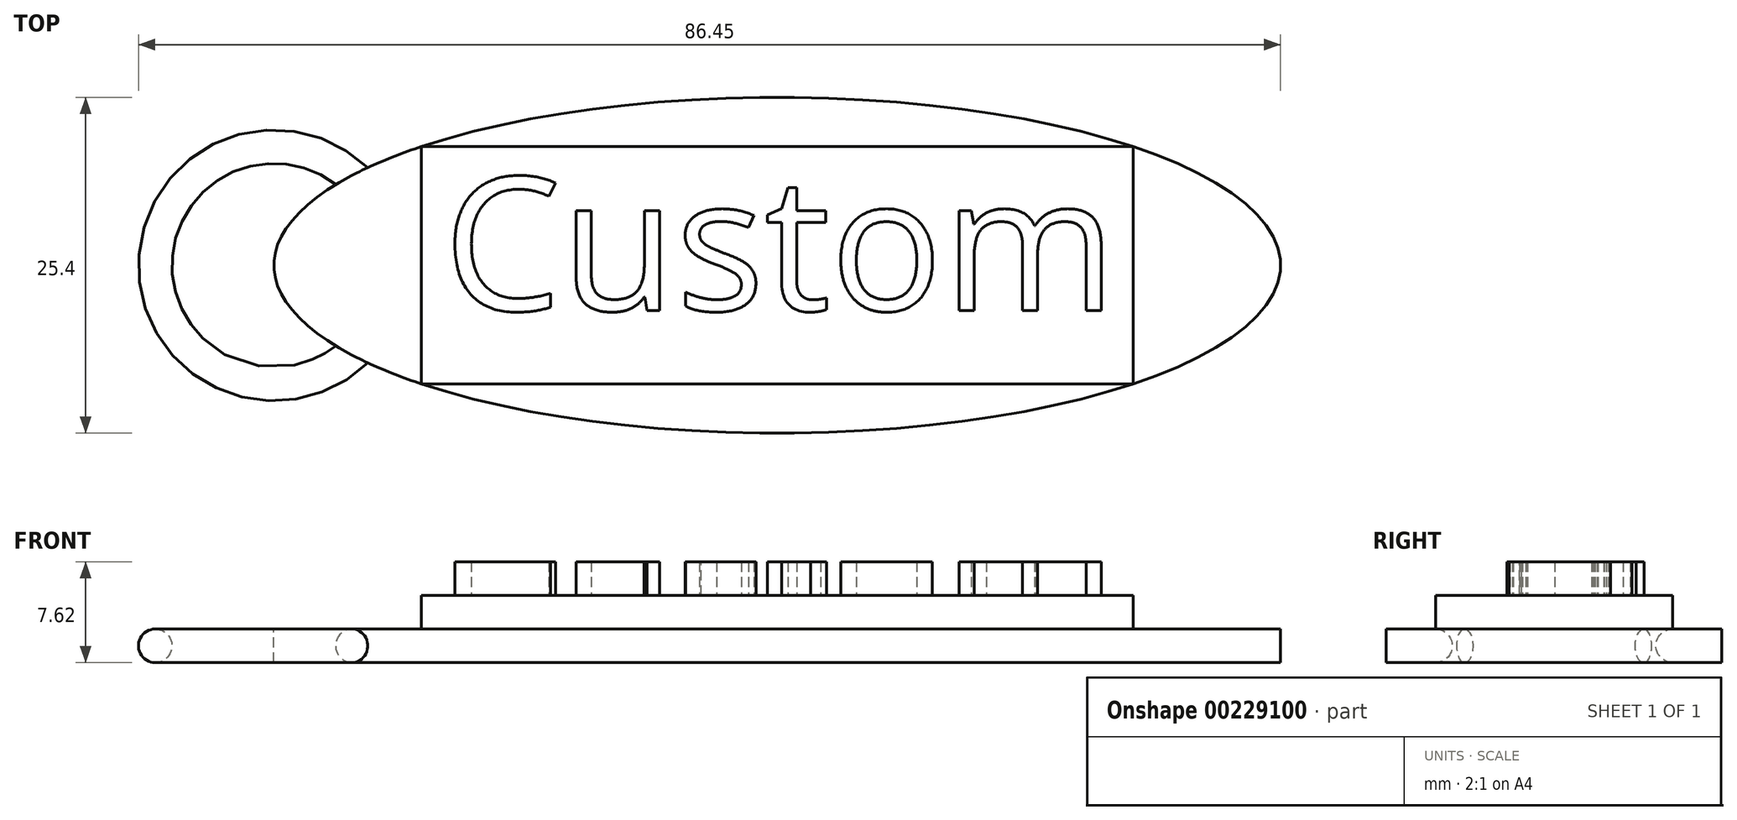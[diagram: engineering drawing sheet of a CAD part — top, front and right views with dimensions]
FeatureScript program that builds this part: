
annotation { "Feature Type Name" : "Feature", "Feature Type Description" : "" }
export const myFeature = defineFeature(function(context is Context, id is Id, definition is map)
    precondition{}
    {
        {
            var Q0;
            Q0=qCreatedBy(makeId("Top.planeOp"),FACE);
            var sketch = newSketch(context, id + "F0", { "sketchPlane" : qUnion([Q0])});
            skLineSegment(sketch, "E0", {"start": v(0, 0) * mm, "end": v(0, 12.7) * mm, "construction": true});
            skLineSegment(sketch, "E1", {"start": v(0, 0) * mm, "end": v(0, -12.7) * mm, "construction": true});
            skLineSegment(sketch, "E2", {"start": v(0, 0) * mm, "end": v(38.1, 0) * mm, "construction": true});
            skLineSegment(sketch, "E3", {"start": v(0, 0) * mm, "end": v(-38.1, 0) * mm, "construction": true});
            skEllipse(sketch, "E4", {"center": v(0, 0) * mm, "majorRadius": 38.1 * mm, "minorRadius": 12.7 * mm, "majorAxis": v(1, 0)});
            skPoint(sketch, "E5", {"position": v(-38.1, 0) * mm});
            skSolve(sketch);
        }
        {
            var Q0;
            Q0=makeQuery(id+"F0.imprint","IMPRINT",FACE,{"disambiguationData":[TD([[makeQuery(id+"F0.imprint","IMPRINT",EDGE,{"derivedFrom":sQuery(id+"F0.wireOp",EDGE,"E4")}),1.0]])]});
            extrude(context, id + "F1", {"entities" : qUnion([Q0]), "depth" : 2.54 * mm});
        }
        {
            var Q0;
            Q0=makeQuery(id+"F1.opExtrude","CAP_FACE",FACE,{"disambiguationData":[OSD([sQuery(id+"F0.wireOp",EDGE,"E4")])],"isStart":false});
            var sketch = newSketch(context, id + "F2", { "sketchPlane" : qUnion([Q0])});
            skLineSegment(sketch, "E6", {"start": v(0, 0) * mm, "end": v(-38.1, 0) * mm, "construction": true});
            skLineSegment(sketch, "E7", {"start": v(-38.1, 0) * mm, "end": v(38.1, 0) * mm, "construction": true});
            skLineSegment(sketch, "E8", {"start": v(0, 0) * mm, "end": v(0, 12.7) * mm, "construction": true});
            skLineSegment(sketch, "E9", {"start": v(0, 12.7) * mm, "end": v(0, -12.7) * mm, "construction": true});
            skLineSegment(sketch, "E10", {"start": v(-38.1, 0) * mm, "end": v(0, 12.7) * mm, "construction": true});
            skLineSegment(sketch, "E11", {"start": v(0, 12.7) * mm, "end": v(38.1, 0) * mm, "construction": true});
            skLineSegment(sketch, "E12", {"start": v(38.1, 0) * mm, "end": v(0, -12.7) * mm, "construction": true});
            skLineSegment(sketch, "E13", {"start": v(0, -12.7) * mm, "end": v(-38.1, 0) * mm, "construction": true});
            skLineSegment(sketch, "E14", {"start": v(0, 0) * mm, "end": v(26.94, -8.98) * mm, "construction": true});
            skLineSegment(sketch, "E15", {"start": v(26.94, -8.98) * mm, "end": v(26.94, 8.98) * mm});
            skLineSegment(sketch, "E16", {"start": v(26.94, 8.98) * mm, "end": v(-26.94, 8.98) * mm});
            skLineSegment(sketch, "E17", {"start": v(-26.94, 8.98) * mm, "end": v(-26.94, -8.98) * mm});
            skLineSegment(sketch, "E18", {"start": v(-26.94, -8.98) * mm, "end": v(26.94, -8.98) * mm});
            skSolve(sketch);
        }
        {
            var Q0;
            Q0=makeQuery(id+"F2.imprint","IMPRINT",FACE,{"disambiguationData":[TD([[makeQuery(id+"F2.imprint","IMPRINT",EDGE,{"derivedFrom":sQuery(id+"F2.wireOp",EDGE,"E15")}),1.0]])]});
            extrude(context, id + "F3", {"entities" : qUnion([Q0]), "operationType" : NewBodyOperationType.ADD, "depth" : 2.54 * mm});
        }
        {
            var Q0;
            Q0=makeQuery(id+"F3.opExtrude","CAP_FACE",FACE,{"disambiguationData":[OSD([sQuery(id+"F2.wireOp",EDGE,"E15"),sQuery(id+"F2.wireOp",EDGE,"E16"),sQuery(id+"F2.wireOp",EDGE,"E17"),sQuery(id+"F2.wireOp",EDGE,"E18")])],"isStart":false});
            var sketch = newSketch(context, id + "F4", { "sketchPlane" : qUnion([Q0])});
            skLineSegment(sketch, "E19", {"start": v(-26.94, 8.98) * mm, "end": v(26.94, -8.98) * mm, "construction": true});
            skLineSegment(sketch, "E20", {"start": v(-26.94, -8.98) * mm, "end": v(26.94, 8.98) * mm, "construction": true});
            skLineSegment(sketch, "E21", {"start": v(-26.94, 0) * mm, "end": v(26.94, 0) * mm, "construction": true});
            skLineSegment(sketch, "E22", {"start": v(0, 8.98) * mm, "end": v(0, -8.98) * mm, "construction": true});
            skLineSegment(sketch, "E23", {"start": v(0, 8.98) * mm, "end": v(-26.94, 0) * mm, "construction": true});
            skLineSegment(sketch, "E24", {"start": v(0, 8.98) * mm, "end": v(26.94, 0) * mm, "construction": true});
            skLineSegment(sketch, "E25", {"start": v(26.94, 0) * mm, "end": v(0, -8.98) * mm, "construction": true});
            skLineSegment(sketch, "E26", {"start": v(0, -8.98) * mm, "end": v(-26.94, 0) * mm, "construction": true});
            skLineSegment(sketch, "E27", {"start": v(-13.47, -4.5) * mm, "end": v(-13.47, -8.98) * mm, "construction": true});
            skLineSegment(sketch, "E28", {"start": v(-13.47, -8.98) * mm, "end": v(-13.47, 8.98) * mm, "construction": true});
            skLineSegment(sketch, "E29", {"start": v(13.47, -4.5) * mm, "end": v(13.47, -8.98) * mm, "construction": true});
            skLineSegment(sketch, "E30", {"start": v(13.47, -8.98) * mm, "end": v(13.47, 8.98) * mm, "construction": true});
            skLineSegment(sketch, "E31", {"start": v(13.47, 8.98) * mm, "end": v(26.94, 0) * mm, "construction": true});
            skLineSegment(sketch, "E32", {"start": v(13.47, 0) * mm, "end": v(26.94, 8.98) * mm, "construction": true});
            skLineSegment(sketch, "E33", {"start": v(26.94, 0) * mm, "end": v(13.47, -8.98) * mm, "construction": true});
            skLineSegment(sketch, "E34", {"start": v(13.47, 0) * mm, "end": v(26.94, -8.98) * mm, "construction": true});
            skLineSegment(sketch, "E35", {"start": v(-26.94, 8.98) * mm, "end": v(-13.47, 0) * mm, "construction": true});
            skLineSegment(sketch, "E36", {"start": v(-13.47, 8.98) * mm, "end": v(-26.94, 0) * mm, "construction": true});
            skLineSegment(sketch, "E37", {"start": v(-13.47, 8.98) * mm, "end": v(0, 0) * mm, "construction": true});
            skLineSegment(sketch, "E38", {"start": v(0, 8.98) * mm, "end": v(-13.47, 0) * mm, "construction": true});
            skLineSegment(sketch, "E39", {"start": v(-26.94, -8.98) * mm, "end": v(-13.47, 0) * mm, "construction": true});
            skLineSegment(sketch, "E40", {"start": v(-26.94, 0) * mm, "end": v(-13.47, -8.98) * mm, "construction": true});
            skLineSegment(sketch, "E41", {"start": v(-13.47, -8.98) * mm, "end": v(0, 0) * mm, "construction": true});
            skLineSegment(sketch, "E42", {"start": v(-13.47, 0) * mm, "end": v(0, -8.98) * mm, "construction": true});
            skLineSegment(sketch, "E43", {"start": v(0, -8.98) * mm, "end": v(13.47, 0) * mm, "construction": true});
            skLineSegment(sketch, "E44", {"start": v(0, 0) * mm, "end": v(13.47, -8.98) * mm, "construction": true});
            skLineSegment(sketch, "E45", {"start": v(0, 8.98) * mm, "end": v(13.47, 0) * mm, "construction": true});
            skLineSegment(sketch, "E46", {"start": v(13.47, 8.98) * mm, "end": v(0, 0) * mm, "construction": true});
            skLineSegment(sketch, "E47", {"start": v(-20.2, 4.5) * mm, "end": v(-20.2, 8.98) * mm, "construction": true});
            skLineSegment(sketch, "E48", {"start": v(-20.2, 8.98) * mm, "end": v(-20.2, -8.98) * mm, "construction": true});
            skLineSegment(sketch, "E49", {"start": v(-6.74, 4.5) * mm, "end": v(-6.74, 8.98) * mm, "construction": true});
            skLineSegment(sketch, "E50", {"start": v(-6.74, 8.98) * mm, "end": v(-6.74, -8.98) * mm, "construction": true});
            skLineSegment(sketch, "E51", {"start": v(6.74, -4.5) * mm, "end": v(6.74, 8.98) * mm, "construction": true});
            skLineSegment(sketch, "E52", {"start": v(6.74, 8.98) * mm, "end": v(6.74, -8.98) * mm, "construction": true});
            skLineSegment(sketch, "E53", {"start": v(20.2, -4.5) * mm, "end": v(20.2, -8.98) * mm, "construction": true});
            skLineSegment(sketch, "E54", {"start": v(20.2, -8.98) * mm, "end": v(20.2, 8.98) * mm, "construction": true});
            skLineSegment(sketch, "E55", {"start": v(20.2, 0) * mm, "end": v(26.94, 8.98) * mm, "construction": true});
            skLineSegment(sketch, "E56", {"start": v(13.47, 0) * mm, "end": v(20.2, 8.98) * mm, "construction": true});
            skLineSegment(sketch, "E57", {"start": v(20.2, 8.98) * mm, "end": v(26.94, 0) * mm, "construction": true});
            skLineSegment(sketch, "E58", {"start": v(20.2, 0) * mm, "end": v(26.94, -8.98) * mm, "construction": true});
            skLineSegment(sketch, "E59", {"start": v(26.94, 0) * mm, "end": v(20.2, -8.98) * mm, "construction": true});
            skLineSegment(sketch, "E60", {"start": v(-26.94, 0) * mm, "end": v(-20.2, -8.98) * mm, "construction": true});
            skLineSegment(sketch, "E61", {"start": v(-26.94, -8.98) * mm, "end": v(-20.2, 0) * mm, "construction": true});
            skLineSegment(sketch, "E62", {"start": v(-26.94, 8.98) * mm, "end": v(-20.2, 0) * mm, "construction": true});
            skLineSegment(sketch, "E63", {"start": v(-20.2, 8.98) * mm, "end": v(-26.94, 0) * mm, "construction": true});
            skLineSegment(sketch, "E64", {"start": v(-20.2, 4.5) * mm, "end": v(-26.94, 4.5) * mm, "construction": true});
            skLineSegment(sketch, "E65", {"start": v(-23.57, 4.5) * mm, "end": v(-23.57, 8.98) * mm, "construction": true});
            skLineSegment(sketch, "E66", {"start": v(-23.57, 8.98) * mm, "end": v(-23.57, -8.98) * mm, "construction": true});
            skLineSegment(sketch, "E67", {"start": v(-23.57, -4.5) * mm, "end": v(-26.94, -4.5) * mm, "construction": true});
            skLineSegment(sketch, "E68", {"start": v(-26.94, -4.5) * mm, "end": v(-20.2, -4.5) * mm, "construction": true});
            skLineSegment(sketch, "E69", {"start": v(23.57, 4.5) * mm, "end": v(26.94, 4.5) * mm, "construction": true});
            skLineSegment(sketch, "E70", {"start": v(26.94, 4.5) * mm, "end": v(20.2, 4.5) * mm, "construction": true});
            skLineSegment(sketch, "E71", {"start": v(23.57, 4.5) * mm, "end": v(23.57, 8.98) * mm, "construction": true});
            skLineSegment(sketch, "E72", {"start": v(23.57, 8.98) * mm, "end": v(23.57, -8.98) * mm, "construction": true});
            skPoint(sketch, "E72.endSnap0", {"position": v(23.57, -4.5) * mm});
            skLineSegment(sketch, "E73", {"start": v(20.2, -4.5) * mm, "end": v(26.94, -4.5) * mm, "construction": true});
            skLineSegment(sketch, "E74", {"start": v(23.57, 8.98) * mm, "end": v(26.94, 4.5) * mm, "construction": true});
            skLineSegment(sketch, "E75", {"start": v(23.57, 4.5) * mm, "end": v(26.94, 8.98) * mm, "construction": true});
            skLineSegment(sketch, "E76", {"start": v(23.57, -4.5) * mm, "end": v(26.94, -8.98) * mm, "construction": true});
            skLineSegment(sketch, "E77", {"start": v(23.57, -8.98) * mm, "end": v(26.94, -4.5) * mm, "construction": true});
            skLineSegment(sketch, "E78", {"start": v(-26.94, -4.5) * mm, "end": v(-23.57, -8.98) * mm, "construction": true});
            skLineSegment(sketch, "E79", {"start": v(-26.94, -8.98) * mm, "end": v(-23.57, -4.5) * mm, "construction": true});
            skLineSegment(sketch, "E80", {"start": v(-26.94, 8.98) * mm, "end": v(-23.57, 4.5) * mm, "construction": true});
            skLineSegment(sketch, "E81", {"start": v(-26.94, 4.5) * mm, "end": v(-23.57, 8.98) * mm, "construction": true});
            skPoint(sketch, "E82", {"position": v(-25.26, 6.74) * mm});
            skPoint(sketch, "E83", {"position": v(-25.26, -6.74) * mm});
            skPoint(sketch, "E84", {"position": v(25.26, 6.74) * mm});
            skPoint(sketch, "E85", {"position": v(25.26, -6.74) * mm});
            skLineSegment(sketch, "E86", {"start": v(-25.26, 6.74) * mm, "end": v(-23.57, 4.5) * mm, "construction": true});
            skLineSegment(sketch, "E87", {"start": v(-25.26, -6.74) * mm, "end": v(-23.57, -4.5) * mm, "construction": true});
            skLineSegment(sketch, "E88", {"start": v(25.26, -6.74) * mm, "end": v(23.57, -4.5) * mm, "construction": true});
            skLineSegment(sketch, "E89", {"start": v(25.26, 6.74) * mm, "end": v(23.57, 4.5) * mm, "construction": true});
            skPoint(sketch, "E90", {"position": v(-24.42, -5.61) * mm});
            skPoint(sketch, "E91", {"position": v(-24.42, 5.61) * mm});
            skPoint(sketch, "E92", {"position": v(24.42, 5.61) * mm});
            skPoint(sketch, "E93", {"position": v(24.42, -5.61) * mm});
            skText(sketch, "E94", { "text": "Custom\n", "fontName": "OpenSans-Regular.ttf"});
            const initialGuessF4  = {"E94": [-0.02526, -0.00342, 1, 0, 0.01016]};
            skSetInitialGuess(sketch, initialGuessF4);
            skSolve(sketch);
        }
        {
            var Q0;
            Q0=makeQuery(id+"F4.imprint","IMPRINT",FACE,{"disambiguationData":[TD([[makeQuery(id+"F4.imprint","IMPRINT",EDGE,{"derivedFrom":sQuery(id+"F4.wireOp",EDGE,"E94.sketch_text.stroke-0")}),-1.0]])]});
            var Q1;
            Q1=makeQuery(id+"F4.imprint","IMPRINT",FACE,{"disambiguationData":[TD([[makeQuery(id+"F4.imprint","IMPRINT",EDGE,{"derivedFrom":sQuery(id+"F4.wireOp",EDGE,"E94.sketch_text.stroke-15")}),-1.0]])]});
            var Q2;
            Q2=makeQuery(id+"F4.imprint","IMPRINT",FACE,{"disambiguationData":[TD([[makeQuery(id+"F4.imprint","IMPRINT",EDGE,{"derivedFrom":sQuery(id+"F4.wireOp",EDGE,"E94.sketch_text.stroke-32")}),-1.0]])]});
            var Q3;
            Q3=makeQuery(id+"F4.imprint","IMPRINT",FACE,{"disambiguationData":[TD([[makeQuery(id+"F4.imprint","IMPRINT",EDGE,{"derivedFrom":sQuery(id+"F4.wireOp",EDGE,"E94.sketch_text.stroke-57")}),-1.0]])]});
            var Q4;
            Q4=makeQuery(id+"F4.imprint","IMPRINT",FACE,{"disambiguationData":[TD([[makeQuery(id+"F4.imprint","IMPRINT",EDGE,{"derivedFrom":sQuery(id+"F4.wireOp",EDGE,"E94.sketch_text.stroke-76")}),-1.0]])]});
            var Q5;
            Q5=makeQuery(id+"F4.imprint","IMPRINT",FACE,{"disambiguationData":[TD([[makeQuery(id+"F4.imprint","IMPRINT",EDGE,{"derivedFrom":sQuery(id+"F4.wireOp",EDGE,"E94.sketch_text.stroke-93")}),-1.0]])]});
            extrude(context, id + "F5", {"entities" : qUnion([Q0, Q1, Q2, Q3, Q4, Q5]), "operationType" : NewBodyOperationType.ADD, "depth" : 2.54 * mm});
        }
        {
            var Q0;
            Q0=qCreatedBy(makeId("Top.planeOp"),FACE);
            var sketch = newSketch(context, id + "F6", { "sketchPlane" : qUnion([Q0])});
            skLineSegment(sketch, "E95", {"start": v(-38.1, 0) * mm, "end": v(-44.45, 0) * mm, "construction": true});
            skLineSegment(sketch, "E96", {"start": v(-38.1, 6.35) * mm, "end": v(-38.1, -6.35) * mm, "construction": true});
            skPoint(sketch, "E97", {"position": v(-38.1, 0) * mm});
            skLineSegment(sketch, "E98", {"start": v(-38.1, -6.35) * mm, "end": v(-44.45, -6.35) * mm, "construction": true});
            skLineSegment(sketch, "E99", {"start": v(-44.45, -6.35) * mm, "end": v(-44.45, 6.35) * mm, "construction": true});
            skLineSegment(sketch, "E100", {"start": v(-44.45, 6.35) * mm, "end": v(-38.1, 6.35) * mm, "construction": true});
            skPoint(sketch, "E101.positionSnap0", {"position": v(-44.45, 0) * mm});
            skLineSegment(sketch, "E102", {"start": v(-38.1, -6.35) * mm, "end": v(-31.75, -6.35) * mm, "construction": true});
            skLineSegment(sketch, "E103", {"start": v(-31.75, -6.35) * mm, "end": v(-31.75, 6.35) * mm, "construction": true});
            skLineSegment(sketch, "E104", {"start": v(-31.75, 6.35) * mm, "end": v(-39.4, 6.35) * mm, "construction": true});
            skArc(sketch, "E105", {"start": v(-31.75, 6.35) * mm, "mid": v(-47.08, 0) * mm, "end": v(-31.75, -6.35) * mm});
            skSolve(sketch);
        }
        {
            var Q0;
            Q0=qCreatedBy(makeId("Top.planeOp"),FACE);
            cPlane(context, id + "F7", {"entities" : qUnion([Q0]), "cplaneType" : CPlaneType.OFFSET, "offset" : 1.27 * mm, "width" : 152.4 * mm, "height" : 152.4 * mm});
        }
        {
            var Q0;
            Q0=qCreatedBy(id+"F7.planeOp",FACE);
            var sketch = newSketch(context, id + "F8", { "sketchPlane" : qUnion([Q0])});
            skArc(sketch, "E106.0", {"start": v(-31.75, 6.35) * mm, "mid": v(-47.08, 0) * mm, "end": v(-31.75, -6.35) * mm});
            skSolve(sketch);
        }
        {
            var Q0;
            Q0=sQuery(id+"F8.wireOp",VERTEX,"E106.0.start");
            var Q1;
            Q1=sQuery(id+"F8.wireOp",EDGE,"E106.0");
            cPlane(context, id + "F9", {"entities" : qUnion([Q0, Q1]), "cplaneType" : CPlaneType.CURVE_POINT, "offset" : 25.4 * mm, "width" : 152.4 * mm, "height" : 152.4 * mm});
        }
        {
            var Q0;
            Q0=qCreatedBy(id+"F9.planeOp",FACE);
            var sketch = newSketch(context, id + "F10", { "sketchPlane" : qUnion([Q0])});
            skCircle(sketch, "E107", {"center": v(17.96, 1.27) * mm, "radius": 1.27 * mm});
            skSolve(sketch);
        }
        {
            var Q0;
            Q0=makeQuery(id+"F10.imprint","IMPRINT",FACE,{"disambiguationData":[TD([[makeQuery(id+"F10.imprint","IMPRINT",EDGE,{"derivedFrom":sQuery(id+"F10.wireOp",EDGE,"E107")}),1.0]])]});
            var Q1;
            Q1=sQuery(id+"F8.wireOp",EDGE,"E106.0");
            sweep(context, id + "F11", {"operationType" : NewBodyOperationType.ADD, "profiles" : qUnion([Q0]), "path" : qUnion([Q1])});
        }
    });
